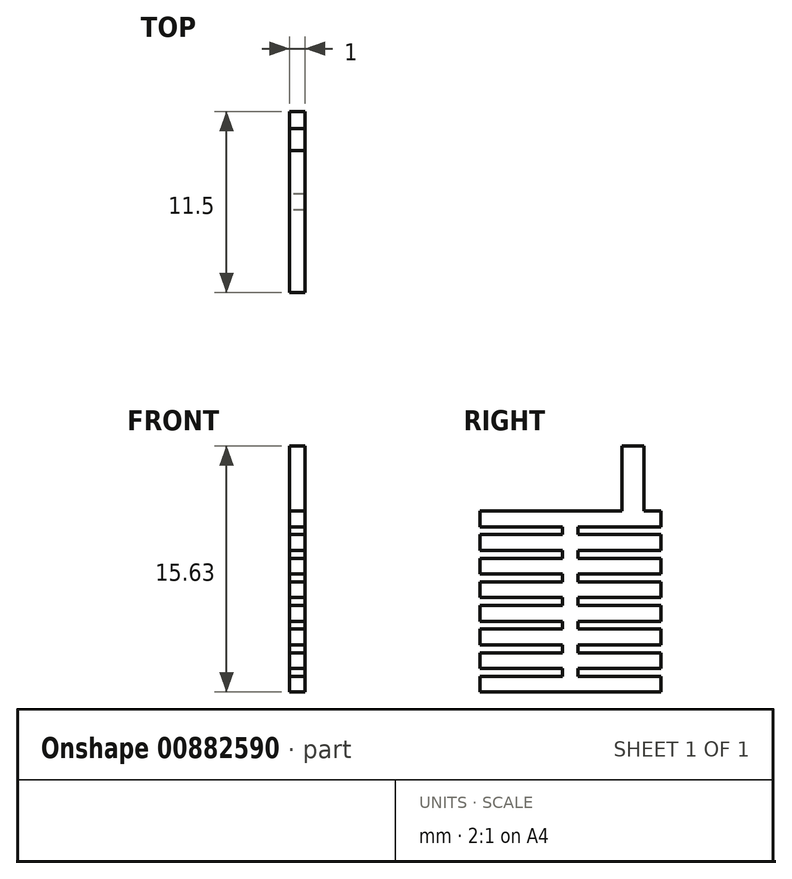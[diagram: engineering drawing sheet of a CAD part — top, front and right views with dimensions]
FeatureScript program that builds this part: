
annotation { "Feature Type Name" : "Feature", "Feature Type Description" : "" }
export const myFeature = defineFeature(function(context is Context, id is Id, definition is map)
    precondition{}
    {
        {
            var Q0;
            Q0=qCreatedBy(makeId("Right.planeOp"),FACE);
            var sketch = newSketch(context, id + "F0", { "sketchPlane" : qUnion([Q0])});
            skLineSegment(sketch, "E0.left", {"start": v(0, 0) * mm, "end": v(0, 0.75) * mm});
            skLineSegment(sketch, "E0.right", {"start": v(11.5, 0) * mm, "end": v(11.5, 0.75) * mm});
            skLineSegment(sketch, "E1", {"start": v(0.25, 10.25) * mm, "end": v(5.25, 10.25) * mm});
            skLineSegment(sketch, "E2.MirrorCS", {"start": v(0.25, 9.75) * mm, "end": v(5.25, 9.75) * mm});
            skLineSegment(sketch, "E3.MirrorCS", {"start": v(5.25, 8.75) * mm, "end": v(0.25, 8.75) * mm});
            skLineSegment(sketch, "E4.MirrorCS", {"start": v(5.25, 8.25) * mm, "end": v(0.25, 8.25) * mm});
            skLineSegment(sketch, "E5.MirrorCS", {"start": v(0.25, 7.25) * mm, "end": v(5.25, 7.25) * mm});
            skLineSegment(sketch, "E6.MirrorCS", {"start": v(0.25, 6.75) * mm, "end": v(5.25, 6.75) * mm});
            skLineSegment(sketch, "E7.MirrorCS", {"start": v(5.25, 5.75) * mm, "end": v(0.25, 5.75) * mm});
            skLineSegment(sketch, "E8.MirrorCS", {"start": v(5.25, 5.25) * mm, "end": v(0.25, 5.25) * mm});
            skLineSegment(sketch, "E9.MirrorCS", {"start": v(0.25, 4.25) * mm, "end": v(5.25, 4.25) * mm});
            skLineSegment(sketch, "E10.MirrorCS", {"start": v(0.25, 3.75) * mm, "end": v(5.25, 3.75) * mm});
            skLineSegment(sketch, "E11.MirrorCS", {"start": v(5.25, 2.75) * mm, "end": v(0.25, 2.75) * mm});
            skLineSegment(sketch, "E12.MirrorCS", {"start": v(5.25, 2.25) * mm, "end": v(0.25, 2.25) * mm});
            skLineSegment(sketch, "E13.MirrorCS", {"start": v(0.25, 1.25) * mm, "end": v(5.25, 1.25) * mm});
            skLineSegment(sketch, "E14.MirrorCS", {"start": v(11.25, 10.25) * mm, "end": v(6.25, 10.25) * mm});
            skLineSegment(sketch, "E15.MirrorCS", {"start": v(11.25, 9.75) * mm, "end": v(6.25, 9.75) * mm});
            skLineSegment(sketch, "E16.MirrorCS", {"start": v(6.25, 8.75) * mm, "end": v(11.25, 8.75) * mm});
            skLineSegment(sketch, "E17.MirrorCS", {"start": v(6.25, 8.25) * mm, "end": v(11.25, 8.25) * mm});
            skLineSegment(sketch, "E18.MirrorCS", {"start": v(11.25, 7.25) * mm, "end": v(6.25, 7.25) * mm});
            skLineSegment(sketch, "E19.MirrorCS", {"start": v(11.25, 6.75) * mm, "end": v(6.25, 6.75) * mm});
            skLineSegment(sketch, "E20.MirrorCS", {"start": v(6.25, 5.75) * mm, "end": v(11.25, 5.75) * mm});
            skLineSegment(sketch, "E21.MirrorCS", {"start": v(6.25, 5.25) * mm, "end": v(11.25, 5.25) * mm});
            skLineSegment(sketch, "E22.MirrorCS", {"start": v(11.25, 4.25) * mm, "end": v(6.25, 4.25) * mm});
            skLineSegment(sketch, "E23.MirrorCS", {"start": v(11.25, 3.75) * mm, "end": v(6.25, 3.75) * mm});
            skLineSegment(sketch, "E24.MirrorCS", {"start": v(6.25, 2.75) * mm, "end": v(11.25, 2.75) * mm});
            skLineSegment(sketch, "E25.MirrorCS", {"start": v(6.25, 2.25) * mm, "end": v(11.25, 2.25) * mm});
            skLineSegment(sketch, "E26.MirrorCS", {"start": v(11.25, 1.25) * mm, "end": v(6.25, 1.25) * mm});
            skLineSegment(sketch, "E27.0", {"start": v(0.25, 0.75) * mm, "end": v(5.25, 0.75) * mm});
            skLineSegment(sketch, "E28", {"start": v(6.25, 0.75) * mm, "end": v(11.25, 0.75) * mm});
            skLineSegment(sketch, "E29.0", {"start": v(5.25, 10.25) * mm, "end": v(5.25, 9.75) * mm});
            skLineSegment(sketch, "E30.0", {"start": v(6.25, 10.25) * mm, "end": v(6.25, 9.75) * mm});
            skPoint(sketch, "E31.orphan", {"position": v(5.75, 0) * mm});
            skLineSegment(sketch, "E32.trimOffspring", {"start": v(5.25, 1.25) * mm, "end": v(5.25, 0.75) * mm});
            skLineSegment(sketch, "E33.trimOffspring", {"start": v(6.25, 1.25) * mm, "end": v(6.25, 0.75) * mm});
            skLineSegment(sketch, "E34.trimOffspring", {"start": v(5.25, 2.75) * mm, "end": v(5.25, 2.25) * mm});
            skLineSegment(sketch, "E35.trimOffspring", {"start": v(6.25, 2.75) * mm, "end": v(6.25, 2.25) * mm});
            skLineSegment(sketch, "E36.trimOffspring", {"start": v(5.25, 4.25) * mm, "end": v(5.25, 3.75) * mm});
            skLineSegment(sketch, "E37.trimOffspring", {"start": v(6.25, 4.25) * mm, "end": v(6.25, 3.75) * mm});
            skLineSegment(sketch, "E38.trimOffspring", {"start": v(5.25, 5.75) * mm, "end": v(5.25, 5.25) * mm});
            skLineSegment(sketch, "E39.trimOffspring", {"start": v(6.25, 5.75) * mm, "end": v(6.25, 5.25) * mm});
            skLineSegment(sketch, "E40.trimOffspring", {"start": v(5.25, 7.25) * mm, "end": v(5.25, 6.75) * mm});
            skLineSegment(sketch, "E41.trimOffspring", {"start": v(6.25, 7.25) * mm, "end": v(6.25, 6.75) * mm});
            skLineSegment(sketch, "E42.trimOffspring", {"start": v(5.25, 8.75) * mm, "end": v(5.25, 8.25) * mm});
            skLineSegment(sketch, "E43.trimOffspring", {"start": v(6.25, 8.75) * mm, "end": v(6.25, 8.25) * mm});
            skPoint(sketch, "E44.orphan", {"position": v(5.75, 11.25) * mm});
            skPoint(sketch, "E45.end.orphan", {"position": v(5.5, 0.75) * mm});
            skPoint(sketch, "E46.orphan", {"position": v(6, 0.75) * mm});
            skLineSegment(sketch, "E47", {"start": v(0.25, 0.75) * mm, "end": v(0, 0.75) * mm});
            skLineSegment(sketch, "E48", {"start": v(0.25, 1.25) * mm, "end": v(0, 1.25) * mm});
            skLineSegment(sketch, "E49.trimOffspring", {"start": v(0, 1.25) * mm, "end": v(0, 2.25) * mm});
            skLineSegment(sketch, "E50", {"start": v(0.25, 2.25) * mm, "end": v(0, 2.25) * mm});
            skLineSegment(sketch, "E51", {"start": v(11.25, 0.75) * mm, "end": v(11.5, 0.75) * mm});
            skLineSegment(sketch, "E52", {"start": v(11.25, 1.25) * mm, "end": v(11.5, 1.25) * mm});
            skLineSegment(sketch, "E53", {"start": v(11.25, 2.25) * mm, "end": v(11.5, 2.25) * mm});
            skLineSegment(sketch, "E54.trimOffspring", {"start": v(11.5, 1.25) * mm, "end": v(11.5, 2.25) * mm});
            skLineSegment(sketch, "E55", {"start": v(11.25, 3.75) * mm, "end": v(11.5, 3.75) * mm});
            skLineSegment(sketch, "E56", {"start": v(11.25, 2.75) * mm, "end": v(11.5, 2.75) * mm});
            skLineSegment(sketch, "E57.trimOffspring", {"start": v(11.5, 2.75) * mm, "end": v(11.5, 3.75) * mm});
            skLineSegment(sketch, "E58", {"start": v(0.25, 3.75) * mm, "end": v(0, 3.75) * mm});
            skLineSegment(sketch, "E59", {"start": v(0, 3.75) * mm, "end": v(0, 2.75) * mm});
            skLineSegment(sketch, "E60", {"start": v(0, 2.75) * mm, "end": v(0.25, 2.75) * mm});
            skLineSegment(sketch, "E61.trimOffspring", {"start": v(0, 2.75) * mm, "end": v(0, 3.75) * mm});
            skLineSegment(sketch, "E62", {"start": v(0.25, 5.25) * mm, "end": v(0, 5.25) * mm});
            skLineSegment(sketch, "E63", {"start": v(0, 5.25) * mm, "end": v(0, 4.25) * mm});
            skLineSegment(sketch, "E64", {"start": v(0, 4.25) * mm, "end": v(0.25, 4.25) * mm});
            skPoint(sketch, "E65.MirrorCS.end.orphan", {"position": v(0.25, 4.25) * mm});
            skLineSegment(sketch, "E66.trimOffspring", {"start": v(0, 4.25) * mm, "end": v(0, 5.25) * mm});
            skLineSegment(sketch, "E67", {"start": v(0.25, 10.25) * mm, "end": v(0, 10.25) * mm});
            skLineSegment(sketch, "E68", {"start": v(0, 10.25) * mm, "end": v(0, 11.25) * mm});
            skPoint(sketch, "E69.end.orphan", {"position": v(0.25, 11.25) * mm});
            skPoint(sketch, "E70.orphan", {"position": v(5.5, 11.25) * mm});
            skPoint(sketch, "E71.start.orphan", {"position": v(6, 11.25) * mm});
            skLineSegment(sketch, "E72", {"start": v(11.25, 10.25) * mm, "end": v(11.5, 10.25) * mm});
            skLineSegment(sketch, "E73", {"start": v(0.25, 5.75) * mm, "end": v(0, 5.75) * mm});
            skLineSegment(sketch, "E74", {"start": v(0, 5.75) * mm, "end": v(0, 6.75) * mm});
            skLineSegment(sketch, "E75", {"start": v(0, 6.75) * mm, "end": v(0.25, 6.75) * mm});
            skLineSegment(sketch, "E76", {"start": v(0.25, 8.25) * mm, "end": v(0, 8.25) * mm});
            skLineSegment(sketch, "E77", {"start": v(0.25, 7.25) * mm, "end": v(0, 7.25) * mm});
            skLineSegment(sketch, "E78.trimOffspring", {"start": v(0, 7.25) * mm, "end": v(0, 8.25) * mm});
            skLineSegment(sketch, "E79", {"start": v(0.25, 9.75) * mm, "end": v(0, 9.75) * mm});
            skLineSegment(sketch, "E80", {"start": v(0.25, 8.75) * mm, "end": v(0, 8.75) * mm});
            skLineSegment(sketch, "E81.trimOffspring", {"start": v(0, 8.75) * mm, "end": v(0, 9.75) * mm});
            skLineSegment(sketch, "E82", {"start": v(11.25, 5.25) * mm, "end": v(11.5, 5.25) * mm});
            skLineSegment(sketch, "E83", {"start": v(11.25, 4.25) * mm, "end": v(11.5, 4.25) * mm});
            skLineSegment(sketch, "E84.trimOffspring", {"start": v(11.5, 4.25) * mm, "end": v(11.5, 6.75) * mm});
            skLineSegment(sketch, "E85", {"start": v(11.25, 6.75) * mm, "end": v(11.5, 6.75) * mm});
            skLineSegment(sketch, "E86", {"start": v(11.25, 5.75) * mm, "end": v(11.5, 5.75) * mm});
            skLineSegment(sketch, "E87", {"start": v(11.25, 8.25) * mm, "end": v(11.5, 8.25) * mm});
            skLineSegment(sketch, "E88", {"start": v(11.25, 7.25) * mm, "end": v(11.5, 7.25) * mm});
            skLineSegment(sketch, "E89.trimOffspring", {"start": v(11.5, 7.25) * mm, "end": v(11.5, 8.25) * mm});
            skLineSegment(sketch, "E90", {"start": v(11.25, 9.75) * mm, "end": v(11.5, 9.75) * mm});
            skLineSegment(sketch, "E91", {"start": v(11.25, 8.75) * mm, "end": v(11.5, 8.75) * mm});
            skLineSegment(sketch, "E92.trimOffspring", {"start": v(11.5, 10.25) * mm, "end": v(11.5, 11.25) * mm});
            skLineSegment(sketch, "E93.trimOffspring", {"start": v(11.5, 8.75) * mm, "end": v(11.5, 9.75) * mm});
            skLineSegment(sketch, "E94", {"start": v(0, 11.25) * mm, "end": v(9.02, 11.25) * mm});
            skLineSegment(sketch, "E95.0", {"start": v(0, -0.25) * mm, "end": v(11.5, -0.25) * mm});
            skLineSegment(sketch, "E96", {"start": v(0, -0.25) * mm, "end": v(0, 0) * mm});
            skLineSegment(sketch, "E97", {"start": v(11.5, -0.25) * mm, "end": v(11.5, 0) * mm});
            skLineSegment(sketch, "E98", {"start": v(10.42, 11.25) * mm, "end": v(10.42, 15.38) * mm});
            skLineSegment(sketch, "E99", {"start": v(10.42, 15.38) * mm, "end": v(9.02, 15.38) * mm});
            skLineSegment(sketch, "E100", {"start": v(9.02, 15.38) * mm, "end": v(9.02, 11.25) * mm});
            skLineSegment(sketch, "E101.trimOffspring", {"start": v(10.42, 11.25) * mm, "end": v(11.5, 11.25) * mm});
            skSolve(sketch);
        }
        {
            var Q0;
            {var subQ2=sQuery(id+"F0.wireOp",EDGE,"E69");Q0=makeQuery(id+"F0.imprint","IMPRINT",FACE,{"disambiguationData":[TD([[makeQuery(id+"F0.imprint","IMPRINT",EDGE,{"derivedFrom":subQ2}),1.0]])]});}
            var Q1;
            Q1=makeQuery(id+"F0.imprint","IMPRINT",FACE,{"disambiguationData":[TD([[makeQuery(id+"F0.imprint","IMPRINT",EDGE,{"derivedFrom":sQuery(id+"F0.wireOp",EDGE,"992a07e8-3ec6-4f7a-80ec-2619e03a62cb0.MirrorCS")}),-1.0]])]});
            var Q2;
            Q2=makeQuery(id+"F0.imprint","IMPRINT",FACE,{"disambiguationData":[TD([[makeQuery(id+"F0.imprint","IMPRINT",EDGE,{"derivedFrom":sQuery(id+"F0.wireOp",EDGE,"E2.MirrorCS")}),-1.0]])]});
            var Q3;
            Q3=makeQuery(id+"F0.imprint","IMPRINT",FACE,{"disambiguationData":[TD([[makeQuery(id+"F0.imprint","IMPRINT",EDGE,{"derivedFrom":sQuery(id+"F0.wireOp",EDGE,"E15.MirrorCS")}),1.0]])]});
            var Q4;
            Q4=makeQuery(id+"F0.imprint","IMPRINT",FACE,{"disambiguationData":[TD([[makeQuery(id+"F0.imprint","IMPRINT",EDGE,{"derivedFrom":sQuery(id+"F0.wireOp",EDGE,"E4.MirrorCS")}),1.0]])]});
            var Q5;
            Q5=makeQuery(id+"F0.imprint","IMPRINT",FACE,{"disambiguationData":[TD([[makeQuery(id+"F0.imprint","IMPRINT",EDGE,{"derivedFrom":sQuery(id+"F0.wireOp",EDGE,"E17.MirrorCS")}),-1.0]])]});
            var Q6;
            Q6=makeQuery(id+"F0.imprint","IMPRINT",FACE,{"disambiguationData":[TD([[makeQuery(id+"F0.imprint","IMPRINT",EDGE,{"derivedFrom":sQuery(id+"F0.wireOp",EDGE,"E6.MirrorCS")}),-1.0]])]});
            var Q7;
            Q7=makeQuery(id+"F0.imprint","IMPRINT",FACE,{"disambiguationData":[TD([[makeQuery(id+"F0.imprint","IMPRINT",EDGE,{"derivedFrom":sQuery(id+"F0.wireOp",EDGE,"a16373e9-d2c6-41f7-816a-453fc2b497b10.MirrorCS")}),1.0]])]});
            var Q8;
            Q8=makeQuery(id+"F0.imprint","IMPRINT",FACE,{"disambiguationData":[TD([[makeQuery(id+"F0.imprint","IMPRINT",EDGE,{"derivedFrom":sQuery(id+"F0.wireOp",EDGE,"E8.MirrorCS")}),1.0]])]});
            var Q9;
            Q9=makeQuery(id+"F0.imprint","IMPRINT",FACE,{"disambiguationData":[TD([[makeQuery(id+"F0.imprint","IMPRINT",EDGE,{"derivedFrom":sQuery(id+"F0.wireOp",EDGE,"d2dfbef5-987c-4325-907b-c1e8b75d7ffa0.MirrorCS")}),1.0]])]});
            var Q10;
            Q10=makeQuery(id+"F0.imprint","IMPRINT",FACE,{"disambiguationData":[TD([[makeQuery(id+"F0.imprint","IMPRINT",EDGE,{"derivedFrom":sQuery(id+"F0.wireOp",EDGE,"E23.MirrorCS")}),1.0]])]});
            var Q11;
            Q11=makeQuery(id+"F0.imprint","IMPRINT",FACE,{"disambiguationData":[TD([[makeQuery(id+"F0.imprint","IMPRINT",EDGE,{"derivedFrom":sQuery(id+"F0.wireOp",EDGE,"E10.MirrorCS")}),-1.0]])]});
            var Q12;
            Q12=makeQuery(id+"F0.imprint","IMPRINT",FACE,{"disambiguationData":[TD([[makeQuery(id+"F0.imprint","IMPRINT",EDGE,{"derivedFrom":sQuery(id+"F0.wireOp",EDGE,"E12.MirrorCS")}),1.0]])]});
            var Q13;
            Q13=makeQuery(id+"F0.imprint","IMPRINT",FACE,{"disambiguationData":[TD([[makeQuery(id+"F0.imprint","IMPRINT",EDGE,{"derivedFrom":sQuery(id+"F0.wireOp",EDGE,"E25.MirrorCS")}),-1.0]])]});
            extrude(context, id + "F1", {"entities" : qUnion([Q0, Q1, Q2, Q3, Q4, Q5, Q6, Q7, Q8, Q9, Q10, Q11, Q12, Q13]), "depth" : 1 * mm, "offsetDistance" : 25 * mm});
        }
    });
